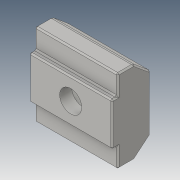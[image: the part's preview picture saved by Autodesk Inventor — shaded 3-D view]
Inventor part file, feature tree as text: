
AUTODESK INVENTOR PART (.ipt)
format: ipt  version: 2016 (Build 200138000, 138)  size: 169,984 bytes
history: native  units: in
note: dims shown in document units (in); Inventor stores cm internally (conversion verified against a paired STEP export)
features: extrude x2, chamfer x2, sketch x2, hole x1
ambient origin geometry x8: Origin, YZ Plane, XZ Plane, XY Plane, X Axis, Y Axis, Z Axis, Center Point
bodies: Solid1 (feature_tree)
feature tree (7):
  extrude  "Extrusion1"  Depth=0.5906in
  extrude  "Extrusion2"  Depth=0.3937in
  hole  "Hole2"  [1 undecoded]
  chamfer  "Chamfer1"  Distance=0.3071in
  chamfer  "Chamfer2"  Distance=0.0394in
  sketch  "Sketch1"  dims[d0=0.5906in d1=0.1181in]
  sketch  "Sketch2"  dims[d2=0.1181in d5=0.3937in d6=0.8919in d7=0.3071in d8=0.0394in d9=0.2362in d10=0.5906in d11=0.0in d12=0.3228in d14=0.189in d15=0.0in d25=0.2953in d26=0.2953in d27=0.2953in d28=0.2953in d29=0.1575in d30=0.75in d31=0.375in d32=0.25in d33=0.5635in d34=1.0in d35=0.8108in d36=0.02in d37=0.125in d38=45.0deg d39=0.01in d40=0.125in d41=45.0deg]
note: 1 required parameter value undecoded (feature->parameter linkage not recoverable at this tier; creation-order binding heuristic only, values carry confidence <= 0.55)
